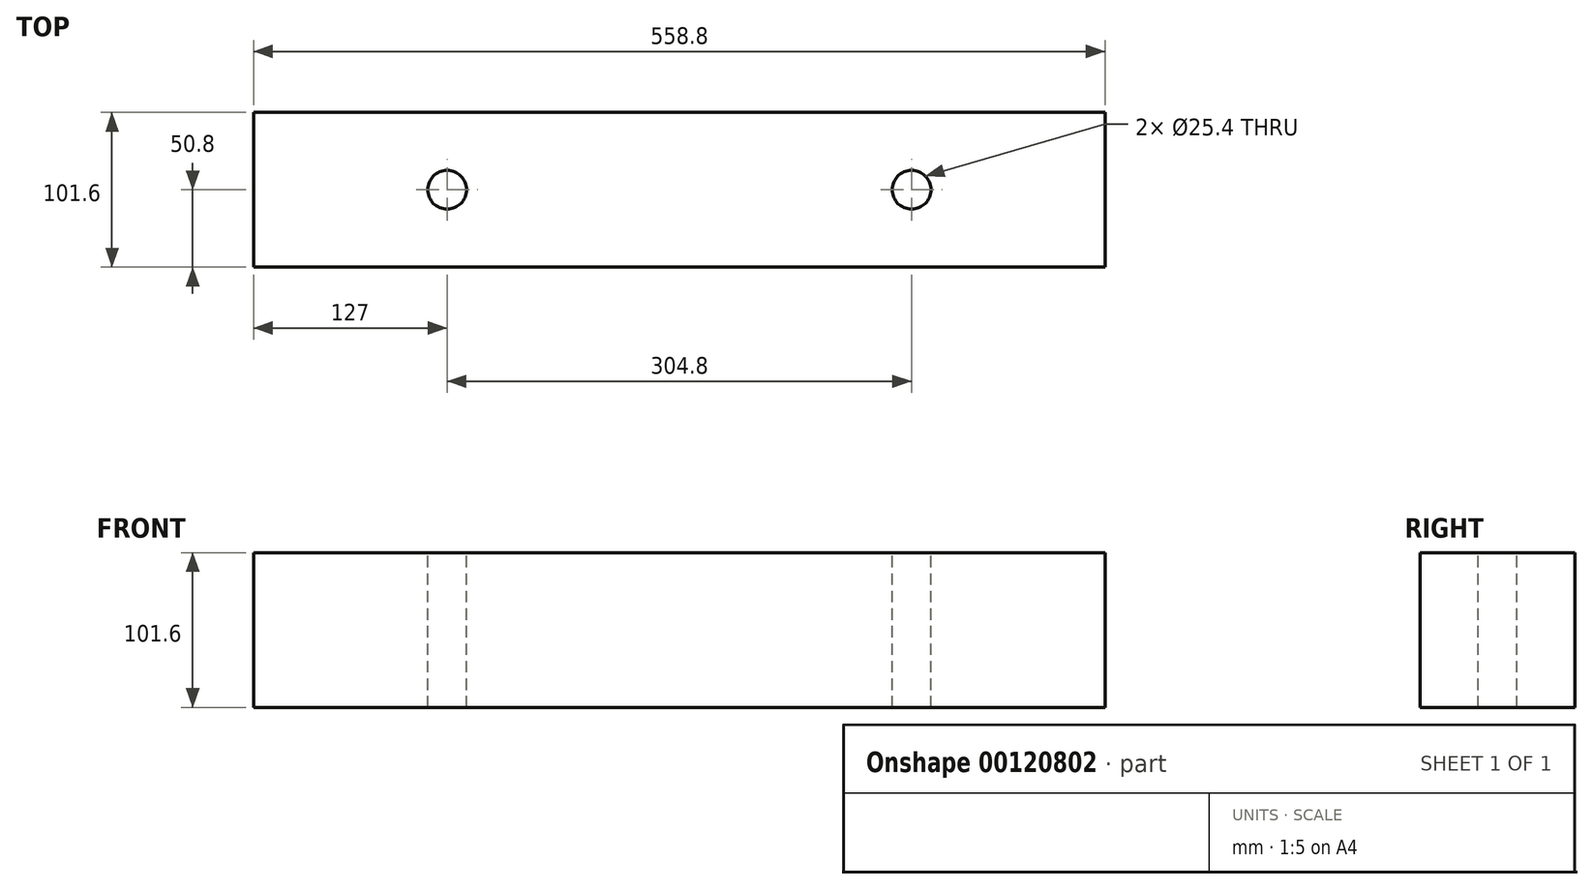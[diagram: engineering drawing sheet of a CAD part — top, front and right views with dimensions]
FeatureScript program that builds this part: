
annotation { "Feature Type Name" : "Feature", "Feature Type Description" : "" }
export const myFeature = defineFeature(function(context is Context, id is Id, definition is map)
    precondition{}
    {
        {
            var Q0;
            Q0=qCreatedBy(makeId("Top.planeOp"),FACE);
            var sketch = newSketch(context, id + "F0", { "sketchPlane" : qUnion([Q0])});
            skLineSegment(sketch, "E0.bottom", {"start": v(0, 0) * mm, "end": v(558.8, 0) * mm});
            skLineSegment(sketch, "E0.top", {"start": v(0, 101.6) * mm, "end": v(558.8, 101.6) * mm});
            skLineSegment(sketch, "E0.left", {"start": v(0, 0) * mm, "end": v(0, 101.6) * mm});
            skLineSegment(sketch, "E0.right", {"start": v(558.8, 0) * mm, "end": v(558.8, 101.6) * mm});
            skSolve(sketch);
        }
        {
            var Q0;
            Q0 = qSketchRegion(id + "F0", true);
            extrude(context, id + "F1", {"entities" : qUnion([Q0]), "oppositeDirection" : true, "depth" : 101.6 * mm});
        }
        {
            var Q0;
            Q0=makeQuery(id+"F1.opExtrude","CAP_FACE",FACE,{"disambiguationData":[OSD([sQuery(id+"F0.wireOp",EDGE,"E0.bottom"),sQuery(id+"F0.wireOp",EDGE,"E0.top"),sQuery(id+"F0.wireOp",EDGE,"E0.left"),sQuery(id+"F0.wireOp",EDGE,"E0.right")])],"isStart":true});
            var sketch = newSketch(context, id + "F2", { "sketchPlane" : qUnion([Q0])});
            skCircle(sketch, "E1", {"center": v(127, 50.8) * mm, "radius": 12.7 * mm});
            skCircle(sketch, "E2", {"center": v(431.8, 50.8) * mm, "radius": 12.7 * mm});
            skLineSegment(sketch, "E3", {"start": v(114.3, 50.8) * mm, "end": v(0, 50.8) * mm});
            skLineSegment(sketch, "E4", {"start": v(431.8, 50.8) * mm, "end": v(558.8, 50.8) * mm});
            skLineSegment(sketch, "E5", {"start": v(127, 63.5) * mm, "end": v(127, 101.6) * mm});
            skLineSegment(sketch, "E6", {"start": v(127, 38.1) * mm, "end": v(127, 0) * mm});
            skSolve(sketch);
        }
        {
            var Q0;
            Q0 = qSketchRegion(id + "F2", true);
            extrude(context, id + "F3", {"entities" : qUnion([Q0]), "operationType" : NewBodyOperationType.REMOVE, "endBound" : BoundingType.THROUGH_ALL, "oppositeDirection" : true, "depth" : 25.4 * mm});
        }
    });
